# Revit family: HUNTER_A2C-1200 Wall Mounted
name_source: partatom
category: Electrical Equipment
revit_build: Autodesk Revit 2017 (Build: 20160225_1515(x64)
units: mm (PartAtom-declared; Revit-internal decimal feet)

## family parameters
Cut with Voids When Loaded = No
Host = Face
OmniClass Number = 23.35.25.21
Panel Configuration = One Column
Part Type = Panelboard
Room Calculation Point = No
Round Connector Dimension = Use Diameter
Shared = Yes

## types (3) — shared parameters
Assembly Code = D5090900
Current = 1 A
Decoders = Expandable Up to 225 with Decoders
Default Elevation = 1200 mm
Enclosure_Depth = 170 mm  [stored 0.557743 ft]
Enclosure_Height = 393 mm
Enclosure_Width = 393 mm
Expansion Module = A2M-600 (6 Stations plug-in) Expansion Module , A2C-F3 (3 input flow meter) expansion module
Input Voltage = 120 V
Keynote = 328423.04
Manufacturer = Hunter® Industries
Number of Sensor Inputs = 3-6 Dedicated Flow Input
Output Voltage = 24 V
Panel Type = Modular
Power = 122 VA
Power factor = 1
Sensor Input = 3 Clik, 3 Flow (expandable to 6), 1 Solar Sync
Stations = 12 Stations base count expandable to 54 Stations
Transformer Output = 24VAC, 4.0A
Type Comments = Hunter's Flagship Controller
Type Image = <None>
URL = https://www.hunterindustries.com
Voltage = 120

## per-type parameters (varying)
| type | Description | Enclosure Material | Model | Protection Rating |
| A2C-1200-M | 12-Station base unit , Wall mounted controller, expandable to 54 stations, with Metal enclosure | Hunter® Metal Grey | A2C-1200-M / A2C-1800-M / A2C-2400-M / A2C-3000-M / A2C-3600-M / A2C-4200-M / A2C-4800-M / A2C-5400-M | IP44 |
| A2C-1200-SS | 12-Station base unit , Wall mounted controller, expandable to 54 stations, with Stainless Steel enclosure | Hunter® Stainless Steel | A2C-1200-SS / A2C-1800-SS / A2C-2400-SS / A2C-3000-SS / A2C-3600-SS / A2C-4200-SS / A2C-4800-SS / A2C-5400-SS | IP44 |
| A2C-1200-P | 12-Station base unit , Wall mounted controller, expandable to 54 stations, with Plastic enclosure | Hunter® Plastic | A2C-1200-P / A2C-1800-P / A2C-2400-P / A2C-3000-P / A2C-3600-P / A2C-4200-P / A2C-4800-P / A2C-5400-P | IP24 |

note: [stored X ft] marks values corroborated as IEEE doubles in the binary element streams (Revit-internal decimal feet)

## geometry (parser evidence)
native form markers: Sweep x4
no freeform markers — native parametric forms only
